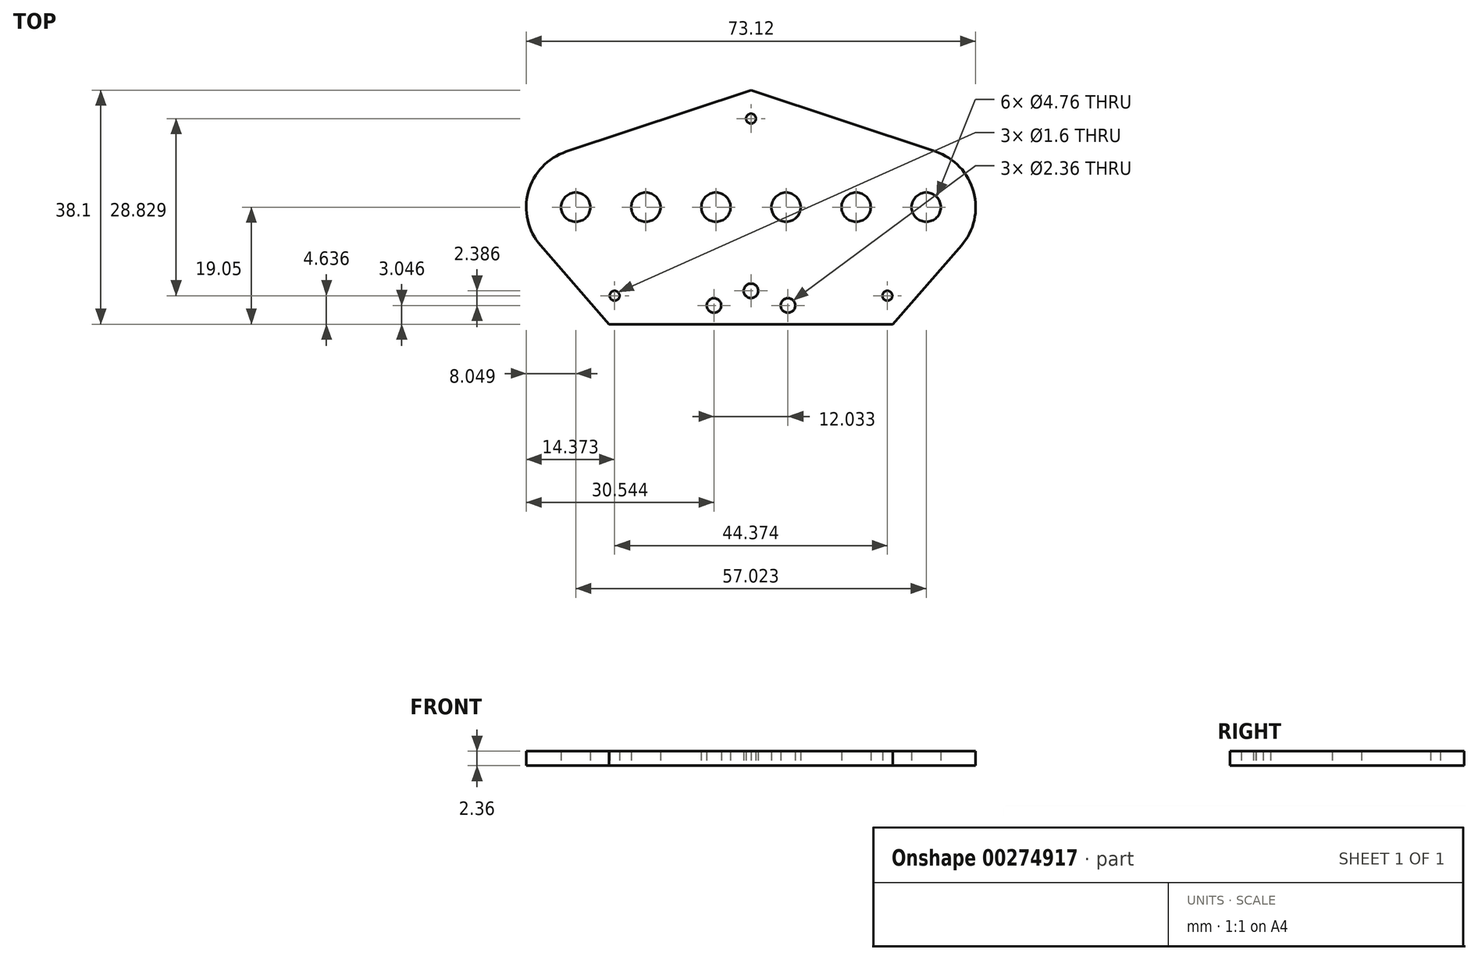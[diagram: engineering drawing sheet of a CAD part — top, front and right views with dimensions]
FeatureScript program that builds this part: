
annotation { "Feature Type Name" : "Feature", "Feature Type Description" : "" }
export const myFeature = defineFeature(function(context is Context, id is Id, definition is map)
    precondition{}
    {
        {
            var Q0;
            Q0=qCreatedBy(makeId("Top.planeOp"),FACE);
            var sketch = newSketch(context, id + "F0", { "sketchPlane" : qUnion([Q0])});
            skCircle(sketch, "E0", {"center": v(5.7, 0) * mm, "radius": 2.38 * mm});
            skCircle(sketch, "E1.1.0.0", {"center": v(17.1, 0) * mm, "radius": 2.38 * mm});
            skCircle(sketch, "E1.2.0.0", {"center": v(28.51, 0) * mm, "radius": 2.38 * mm});
            skLineSegment(sketch, "E1.direction1", {"start": v(5.7, 0) * mm, "end": v(17.1, 0) * mm, "construction": true});
            skLineSegment(sketch, "E2.0", {"start": v(0, -19.05) * mm, "end": v(23.06, -19.05) * mm});
            skCircle(sketch, "E3", {"center": v(0, 14.41) * mm, "radius": 0.8 * mm});
            skCircle(sketch, "E4", {"center": v(22.19, -14.41) * mm, "radius": 0.8 * mm});
            skArc(sketch, "E5", {"start": v(34.22, -6.26) * mm, "mid": v(36.23, 2.5) * mm, "end": v(30.05, 9.04) * mm});
            skLineSegment(sketch, "E6", {"start": v(0, 19.05) * mm, "end": v(30.05, 9.04) * mm});
            skLineSegment(sketch, "E7", {"start": v(23.06, -19.05) * mm, "end": v(34.22, -6.26) * mm});
            skLineSegment(sketch, "E8.MirrorCS", {"start": v(0, 19.05) * mm, "end": v(-30.05, 9.04) * mm});
            skArc(sketch, "E9.MirrorCS", {"start": v(-34.22, -6.26) * mm, "mid": v(-36.23, 2.5) * mm, "end": v(-30.05, 9.04) * mm});
            skLineSegment(sketch, "E10.MirrorCS", {"start": v(-23.06, -19.05) * mm, "end": v(-34.22, -6.26) * mm});
            skLineSegment(sketch, "E11.MirrorCS", {"start": v(0, -19.05) * mm, "end": v(-23.06, -19.05) * mm});
            skCircle(sketch, "E12.MirrorC", {"center": v(-22.19, -14.41) * mm, "radius": 0.8 * mm});
            skLineSegment(sketch, "E13.MirrorCS", {"start": v(0, 0) * mm, "end": v(-36.56, 0) * mm, "construction": true});
            skCircle(sketch, "E14.MirrorC", {"center": v(-5.7, 0) * mm, "radius": 2.38 * mm});
            skCircle(sketch, "E15.MirrorC", {"center": v(-17.1, 0) * mm, "radius": 2.38 * mm});
            skCircle(sketch, "E16.MirrorC", {"center": v(-28.51, 0) * mm, "radius": 2.38 * mm});
            skLineSegment(sketch, "E17.MirrorCS", {"start": v(-5.7, 0) * mm, "end": v(-17.1, 0) * mm, "construction": true});
            skCircle(sketch, "E18", {"center": v(0, -13.62) * mm, "radius": 1.18 * mm});
            skCircle(sketch, "E19", {"center": v(6.02, -16) * mm, "radius": 1.18 * mm});
            skCircle(sketch, "E20.MirrorC", {"center": v(-6.02, -16) * mm, "radius": 1.18 * mm});
            skSolve(sketch);
        }
        {
            var Q0;
            Q0 = qSketchRegion(id + "F0", true);
            extrude(context, id + "F1", {"entities" : qUnion([Q0]), "depth" : 2.36 * mm});
        }
    });
